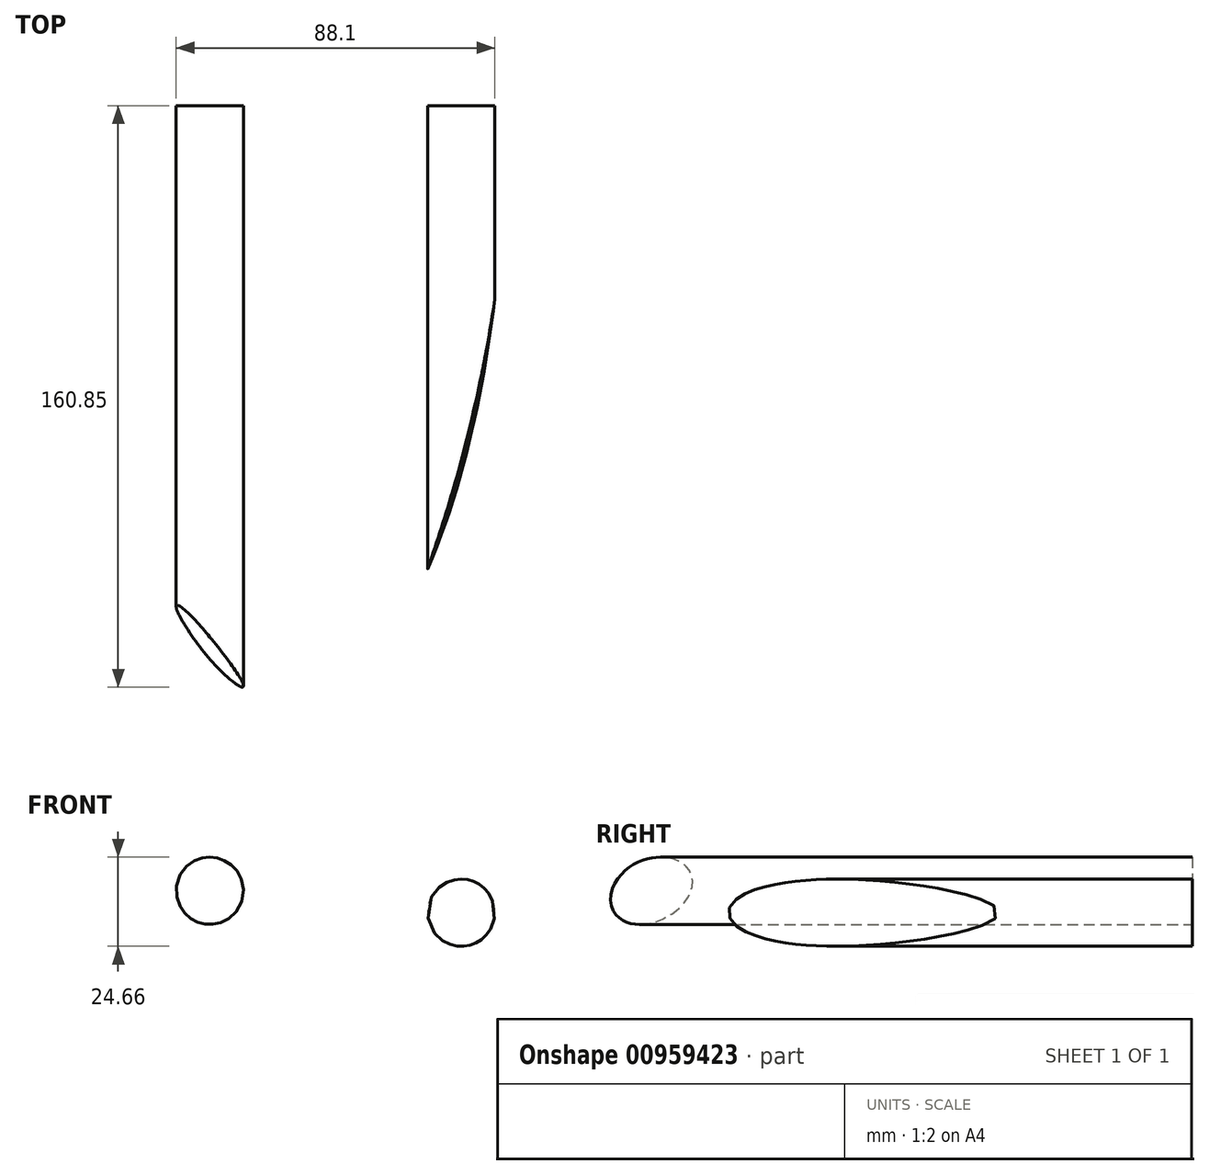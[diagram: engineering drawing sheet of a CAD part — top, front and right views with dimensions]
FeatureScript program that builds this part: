
annotation { "Feature Type Name" : "Feature", "Feature Type Description" : "" }
export const myFeature = defineFeature(function(context is Context, id is Id, definition is map)
    precondition{}
    {
        {
            var Q0;
            Q0=qCreatedBy(makeId("Front.planeOp"),FACE);
            var sketch = newSketch(context, id + "F0", { "sketchPlane" : qUnion([Q0])});
            skCircle(sketch, "E0", {"center": v(0, 0) * mm, "radius": 63.5 * mm});
            skLineSegment(sketch, "E1.0", {"start": v(40.6, 23.44) * mm, "end": v(40.6, -23.44) * mm, "construction": true});
            skLineSegment(sketch, "E1.1", {"start": v(40.6, -23.44) * mm, "end": v(0, -46.87) * mm, "construction": true});
            skLineSegment(sketch, "E1.2", {"start": v(0, -46.87) * mm, "end": v(-40.6, -23.44) * mm, "construction": true});
            skLineSegment(sketch, "E1.3", {"start": v(-40.6, -23.44) * mm, "end": v(-40.6, 23.44) * mm, "construction": true});
            skLineSegment(sketch, "E1.4", {"start": v(-40.6, 23.44) * mm, "end": v(0, 46.87) * mm, "construction": true});
            skLineSegment(sketch, "E1.5", {"start": v(0, 46.87) * mm, "end": v(40.6, 23.44) * mm, "construction": true});
            skPoint(sketch, "E1.0.midPoint", {"position": v(40.6, 0) * mm});
            skCircle(sketch, "E2", {"center": v(0, 0) * mm, "radius": 56.17 * mm, "construction": true});
            skCircle(sketch, "E3", {"center": v(0, 46.87) * mm, "radius": 9.3 * mm});
            skCircle(sketch, "E4", {"center": v(-40.6, 23.44) * mm, "radius": 9.3 * mm});
            skCircle(sketch, "E5", {"center": v(-40.6, -23.44) * mm, "radius": 9.3 * mm});
            skCircle(sketch, "E6", {"center": v(0, -46.87) * mm, "radius": 9.3 * mm});
            skCircle(sketch, "E7", {"center": v(40.6, -23.44) * mm, "radius": 9.3 * mm});
            skCircle(sketch, "E8", {"center": v(40.6, 23.44) * mm, "radius": 9.3 * mm});
            skCircle(sketch, "E9", {"center": v(-23.44, 40.6) * mm, "radius": 9.3 * mm});
            skCircle(sketch, "E10", {"center": v(-46.87, 0) * mm, "radius": 9.3 * mm});
            skCircle(sketch, "E11", {"center": v(-23.44, -40.6) * mm, "radius": 9.3 * mm});
            skLineSegment(sketch, "E12", {"start": v(-40.6, 23.44) * mm, "end": v(40.6, 23.44) * mm, "construction": true});
            skLineSegment(sketch, "E13", {"start": v(-40.6, -23.44) * mm, "end": v(40.6, -23.44) * mm, "construction": true});
            skCircle(sketch, "E14", {"center": v(23.44, 40.6) * mm, "radius": 9.3 * mm});
            skCircle(sketch, "E15", {"center": v(23.44, -40.6) * mm, "radius": 9.3 * mm});
            skCircle(sketch, "E16.MirrorC", {"center": v(46.87, 0) * mm, "radius": 9.3 * mm});
            skLineSegment(sketch, "E17", {"start": v(0, 0) * mm, "end": v(-28.09, 48.64) * mm});
            skLineSegment(sketch, "E18", {"start": v(0, 0) * mm, "end": v(28.09, -48.64) * mm});
            skLineSegment(sketch, "E19", {"start": v(0, 0) * mm, "end": v(-28.09, -48.64) * mm});
            skLineSegment(sketch, "E20", {"start": v(0, 0) * mm, "end": v(28.09, 48.64) * mm});
            skCircle(sketch, "E21", {"center": v(-22.64, 6.07) * mm, "radius": 9.3 * mm});
            skLineSegment(sketch, "E22.anchor1", {"start": v(0, 0) * mm, "end": v(-22.64, 6.07) * mm, "construction": true});
            skLineSegment(sketch, "E22.anchor2", {"start": v(0, 0) * mm, "end": v(-22.64, 6.07) * mm, "construction": true});
            skCircle(sketch, "E23.1.0", {"center": v(-16.57, -16.57) * mm, "radius": 9.3 * mm});
            skCircle(sketch, "E23.2.0", {"center": v(6.07, -22.64) * mm, "radius": 9.3 * mm});
            skCircle(sketch, "E24.1.3.0", {"center": v(22.64, -6.07) * mm, "radius": 9.3 * mm});
            skCircle(sketch, "E24.1.4.0", {"center": v(16.57, 16.57) * mm, "radius": 9.3 * mm});
            skCircle(sketch, "E24.1.5.0", {"center": v(-6.07, 22.64) * mm, "radius": 9.3 * mm});
            skSolve(sketch);
        }
        {
            var Q0;
            Q0=makeQuery(id+"F0.imprint","IMPRINT",FACE,{"disambiguationData":[TD([[makeQuery(id+"F0.imprint","IMPRINT",EDGE,{"derivedFrom":sQuery(id+"F0.wireOp",EDGE,"E10")}),1.0]])]});
            var Q1;
            Q1=makeQuery(id+"F0.imprint","IMPRINT",FACE,{"disambiguationData":[TD([[makeQuery(id+"F0.imprint","IMPRINT",EDGE,{"derivedFrom":sQuery(id+"F0.wireOp",EDGE,"E5")}),1.0]])]});
            var Q2;
            {var subQ0=sQuery(id+"F0.wireOp",EDGE,"E19");var subQ1=sQuery(id+"F0.wireOp",EDGE,"E11");var subQ2=makeQuery(id+"F0.imprint","INTERSECT",VERTEX,{"disambiguationData":[OD(0.0)],"derivedFrom":[subQ1,subQ0]});Q2=makeQuery(id+"F0.imprint","IMPRINT",FACE,{"disambiguationData":[TD([[makeQuery(id+"F0.imprint","IMPRINT",EDGE,{"disambiguationData":[TD([[subQ2,1.0]])],"derivedFrom":subQ1}),1.0]])]});}
            var Q3;
            {var subQ0=sQuery(id+"F0.wireOp",EDGE,"E19");var subQ1=sQuery(id+"F0.wireOp",EDGE,"E11");var subQ2=makeQuery(id+"F0.imprint","INTERSECT",VERTEX,{"disambiguationData":[OD(0.0)],"derivedFrom":[subQ1,subQ0]});Q3=makeQuery(id+"F0.imprint","IMPRINT",FACE,{"disambiguationData":[TD([[makeQuery(id+"F0.imprint","IMPRINT",EDGE,{"disambiguationData":[TD([[subQ2,-1.0]])],"derivedFrom":subQ1}),1.0]])]});}
            var Q4;
            Q4=makeQuery(id+"F0.imprint","IMPRINT",FACE,{"disambiguationData":[TD([[makeQuery(id+"F0.imprint","IMPRINT",EDGE,{"derivedFrom":sQuery(id+"F0.wireOp",EDGE,"E6")}),1.0]])]});
            var Q5;
            {var subQ0=sQuery(id+"F0.wireOp",EDGE,"E18");var subQ1=sQuery(id+"F0.wireOp",EDGE,"E15");var subQ2=makeQuery(id+"F0.imprint","INTERSECT",VERTEX,{"disambiguationData":[OD(0.0)],"derivedFrom":[subQ1,subQ0]});Q5=makeQuery(id+"F0.imprint","IMPRINT",FACE,{"disambiguationData":[TD([[makeQuery(id+"F0.imprint","IMPRINT",EDGE,{"disambiguationData":[TD([[subQ2,-1.0]])],"derivedFrom":subQ1}),1.0]])]});}
            var Q6;
            {var subQ0=sQuery(id+"F0.wireOp",EDGE,"E18");var subQ1=sQuery(id+"F0.wireOp",EDGE,"E15");var subQ2=makeQuery(id+"F0.imprint","INTERSECT",VERTEX,{"disambiguationData":[OD(0.0)],"derivedFrom":[subQ1,subQ0]});Q6=makeQuery(id+"F0.imprint","IMPRINT",FACE,{"disambiguationData":[TD([[makeQuery(id+"F0.imprint","IMPRINT",EDGE,{"disambiguationData":[TD([[subQ2,1.0]])],"derivedFrom":subQ1}),1.0]])]});}
            var Q7;
            Q7=makeQuery(id+"F0.imprint","IMPRINT",FACE,{"disambiguationData":[TD([[makeQuery(id+"F0.imprint","IMPRINT",EDGE,{"derivedFrom":sQuery(id+"F0.wireOp",EDGE,"E7")}),1.0]])]});
            var Q8;
            Q8=makeQuery(id+"F0.imprint","IMPRINT",FACE,{"disambiguationData":[TD([[makeQuery(id+"F0.imprint","IMPRINT",EDGE,{"derivedFrom":sQuery(id+"F0.wireOp",EDGE,"E16.MirrorC")}),-1.0]])]});
            var Q9;
            Q9=makeQuery(id+"F0.imprint","IMPRINT",FACE,{"disambiguationData":[TD([[makeQuery(id+"F0.imprint","IMPRINT",EDGE,{"derivedFrom":sQuery(id+"F0.wireOp",EDGE,"E8")}),1.0]])]});
            var Q10;
            {var subQ0=sQuery(id+"F0.wireOp",EDGE,"E20");var subQ1=sQuery(id+"F0.wireOp",EDGE,"E14");var subQ2=makeQuery(id+"F0.imprint","INTERSECT",VERTEX,{"disambiguationData":[OD(0.0)],"derivedFrom":[subQ1,subQ0]});Q10=makeQuery(id+"F0.imprint","IMPRINT",FACE,{"disambiguationData":[TD([[makeQuery(id+"F0.imprint","IMPRINT",EDGE,{"disambiguationData":[TD([[subQ2,1.0]])],"derivedFrom":subQ1}),1.0]])]});}
            var Q11;
            {var subQ0=sQuery(id+"F0.wireOp",EDGE,"E20");var subQ1=sQuery(id+"F0.wireOp",EDGE,"E14");var subQ2=makeQuery(id+"F0.imprint","INTERSECT",VERTEX,{"disambiguationData":[OD(0.0)],"derivedFrom":[subQ1,subQ0]});Q11=makeQuery(id+"F0.imprint","IMPRINT",FACE,{"disambiguationData":[TD([[makeQuery(id+"F0.imprint","IMPRINT",EDGE,{"disambiguationData":[TD([[subQ2,-1.0]])],"derivedFrom":subQ1}),1.0]])]});}
            var Q12;
            Q12=makeQuery(id+"F0.imprint","IMPRINT",FACE,{"disambiguationData":[TD([[makeQuery(id+"F0.imprint","IMPRINT",EDGE,{"derivedFrom":sQuery(id+"F0.wireOp",EDGE,"E3")}),1.0]])]});
            var Q13;
            {var subQ0=sQuery(id+"F0.wireOp",EDGE,"E17");var subQ1=sQuery(id+"F0.wireOp",EDGE,"E9");var subQ2=makeQuery(id+"F0.imprint","INTERSECT",VERTEX,{"disambiguationData":[OD(0.0)],"derivedFrom":[subQ1,subQ0]});Q13=makeQuery(id+"F0.imprint","IMPRINT",FACE,{"disambiguationData":[TD([[makeQuery(id+"F0.imprint","IMPRINT",EDGE,{"disambiguationData":[TD([[subQ2,-1.0]])],"derivedFrom":subQ1}),1.0]])]});}
            var Q14;
            {var subQ0=sQuery(id+"F0.wireOp",EDGE,"E17");var subQ1=sQuery(id+"F0.wireOp",EDGE,"E9");var subQ2=makeQuery(id+"F0.imprint","INTERSECT",VERTEX,{"disambiguationData":[OD(0.0)],"derivedFrom":[subQ1,subQ0]});Q14=makeQuery(id+"F0.imprint","IMPRINT",FACE,{"disambiguationData":[TD([[makeQuery(id+"F0.imprint","IMPRINT",EDGE,{"disambiguationData":[TD([[subQ2,1.0]])],"derivedFrom":subQ1}),1.0]])]});}
            var Q15;
            Q15=makeQuery(id+"F0.imprint","IMPRINT",FACE,{"disambiguationData":[TD([[makeQuery(id+"F0.imprint","IMPRINT",EDGE,{"derivedFrom":sQuery(id+"F0.wireOp",EDGE,"E4")}),1.0]])]});
            var Q16;
            Q16=makeQuery(id+"F0.imprint","IMPRINT",FACE,{"disambiguationData":[TD([[makeQuery(id+"F0.imprint","IMPRINT",EDGE,{"derivedFrom":sQuery(id+"F0.wireOp",EDGE,"E21")}),1.0]])]});
            var Q17;
            {var subQ0=sQuery(id+"F0.wireOp",EDGE,"E23.1.0");var subQ1=sQuery(id+"F0.wireOp",EDGE,"E19");var subQ2=makeQuery(id+"F0.imprint","INTERSECT",VERTEX,{"disambiguationData":[OD(0.0)],"derivedFrom":[subQ1,subQ0]});Q17=makeQuery(id+"F0.imprint","IMPRINT",FACE,{"disambiguationData":[TD([[makeQuery(id+"F0.imprint","IMPRINT",EDGE,{"disambiguationData":[TD([[subQ2,1.0]])],"derivedFrom":subQ1}),-1.0]])]});}
            var Q18;
            {var subQ0=sQuery(id+"F0.wireOp",EDGE,"E23.1.0");var subQ1=sQuery(id+"F0.wireOp",EDGE,"E19");var subQ2=makeQuery(id+"F0.imprint","INTERSECT",VERTEX,{"disambiguationData":[OD(0.0)],"derivedFrom":[subQ1,subQ0]});Q18=makeQuery(id+"F0.imprint","IMPRINT",FACE,{"disambiguationData":[TD([[makeQuery(id+"F0.imprint","IMPRINT",EDGE,{"disambiguationData":[TD([[subQ2,1.0]])],"derivedFrom":subQ1}),1.0]])]});}
            var Q19;
            {var subQ0=sQuery(id+"F0.wireOp",EDGE,"E23.2.0");var subQ1=sQuery(id+"F0.wireOp",EDGE,"E18");var subQ2=makeQuery(id+"F0.imprint","INTERSECT",VERTEX,{"disambiguationData":[OD(0.0)],"derivedFrom":[subQ1,subQ0]});Q19=makeQuery(id+"F0.imprint","IMPRINT",FACE,{"disambiguationData":[TD([[makeQuery(id+"F0.imprint","IMPRINT",EDGE,{"disambiguationData":[TD([[subQ2,-1.0]])],"derivedFrom":subQ1}),-1.0]])]});}
            var Q20;
            {var subQ0=sQuery(id+"F0.wireOp",EDGE,"E23.2.0");var subQ1=sQuery(id+"F0.wireOp",EDGE,"E18");var subQ2=makeQuery(id+"F0.imprint","INTERSECT",VERTEX,{"disambiguationData":[OD(0.0)],"derivedFrom":[subQ1,subQ0]});Q20=makeQuery(id+"F0.imprint","IMPRINT",FACE,{"disambiguationData":[TD([[makeQuery(id+"F0.imprint","IMPRINT",EDGE,{"disambiguationData":[TD([[subQ2,-1.0]])],"derivedFrom":subQ1}),1.0]])]});}
            var Q21;
            Q21=makeQuery(id+"F0.imprint","IMPRINT",FACE,{"disambiguationData":[TD([[makeQuery(id+"F0.imprint","IMPRINT",EDGE,{"derivedFrom":sQuery(id+"F0.wireOp",EDGE,"E24.1.3.0")}),1.0]])]});
            var Q22;
            {var subQ0=sQuery(id+"F0.wireOp",EDGE,"E24.1.4.0");var subQ1=sQuery(id+"F0.wireOp",EDGE,"E20");var subQ2=makeQuery(id+"F0.imprint","INTERSECT",VERTEX,{"disambiguationData":[OD(0.0)],"derivedFrom":[subQ1,subQ0]});Q22=makeQuery(id+"F0.imprint","IMPRINT",FACE,{"disambiguationData":[TD([[makeQuery(id+"F0.imprint","IMPRINT",EDGE,{"disambiguationData":[TD([[subQ2,-1.0]])],"derivedFrom":subQ1}),-1.0]])]});}
            var Q23;
            {var subQ0=sQuery(id+"F0.wireOp",EDGE,"E24.1.4.0");var subQ1=sQuery(id+"F0.wireOp",EDGE,"E20");var subQ2=makeQuery(id+"F0.imprint","INTERSECT",VERTEX,{"disambiguationData":[OD(0.0)],"derivedFrom":[subQ1,subQ0]});Q23=makeQuery(id+"F0.imprint","IMPRINT",FACE,{"disambiguationData":[TD([[makeQuery(id+"F0.imprint","IMPRINT",EDGE,{"disambiguationData":[TD([[subQ2,-1.0]])],"derivedFrom":subQ1}),1.0]])]});}
            var Q24;
            {var subQ0=sQuery(id+"F0.wireOp",EDGE,"E24.1.5.0");var subQ1=sQuery(id+"F0.wireOp",EDGE,"E17");var subQ2=makeQuery(id+"F0.imprint","INTERSECT",VERTEX,{"disambiguationData":[OD(0.0)],"derivedFrom":[subQ1,subQ0]});Q24=makeQuery(id+"F0.imprint","IMPRINT",FACE,{"disambiguationData":[TD([[makeQuery(id+"F0.imprint","IMPRINT",EDGE,{"disambiguationData":[TD([[subQ2,1.0]])],"derivedFrom":subQ1}),-1.0]])]});}
            var Q25;
            {var subQ0=sQuery(id+"F0.wireOp",EDGE,"E24.1.5.0");var subQ1=sQuery(id+"F0.wireOp",EDGE,"E17");var subQ2=makeQuery(id+"F0.imprint","INTERSECT",VERTEX,{"disambiguationData":[OD(0.0)],"derivedFrom":[subQ1,subQ0]});Q25=makeQuery(id+"F0.imprint","IMPRINT",FACE,{"disambiguationData":[TD([[makeQuery(id+"F0.imprint","IMPRINT",EDGE,{"disambiguationData":[TD([[subQ2,1.0]])],"derivedFrom":subQ1}),1.0]])]});}
            extrude(context, id + "F1", {"entities" : qUnion([Q0, Q1, Q2, Q3, Q4, Q5, Q6, Q7, Q8, Q9, Q10, Q11, Q12, Q13, Q14, Q15, Q16, Q17, Q18, Q19, Q20, Q21, Q22, Q23, Q24, Q25]), "depth" : 254 * mm, "offsetDistance" : 25.4 * mm});
        }
        {
            var Q0;
            Q0=qCreatedBy(makeId("Right.planeOp"),FACE);
            var sketch = newSketch(context, id + "F2", { "sketchPlane" : qUnion([Q0])});
            skLineSegment(sketch, "E25", {"start": v(0, 0) * mm, "end": v(0, 59.35) * mm});
            skEllipticalArc(sketch, "E26", {});
            skLineSegment(sketch, "E27", {"start": v(0, 0) * mm, "end": v(-165.62, 0) * mm});
            skPoint(sketch, "E28.orphan", {"position": v(165.62, 0) * mm});
            const initialGuessF2  = {"E26": [0, 0, 0, 1, 0.059354919940233224, 0.16561861336231232, 6.283185307179586, 1.5707963267948966]};
            skSetInitialGuess(sketch, initialGuessF2);
            skSolve(sketch);
        }
        {
            var Q0;
            Q0=makeQuery(id+"F2.imprint","IMPRINT",FACE,{"disambiguationData":[TD([[makeQuery(id+"F2.imprint","IMPRINT",EDGE,{"derivedFrom":sQuery(id+"F2.wireOp",EDGE,"E25")}),1.0]])]});
            var Q1;
            Q1=sQuery(id+"F2.wireOp",EDGE,"E27");
            revolve(context, id + "F3", {"surfaceOperationType" : NewSurfaceOperationType.NEW, "entities" : qUnion([Q0]), "axis" : qUnion([Q1]), "revolveType" : RevolveType.FULL});
        }
        {
            var Q0;
            Q0=makeQuery(id+"F1.opExtrude","SWEPT_BODY",BODY,{"disambiguationData":[OSD([sQuery(id+"F0.wireOp",EDGE,"E9")])]});
            var Q1;
            Q1=makeQuery(id+"F1.opExtrude","SWEPT_BODY",BODY,{"disambiguationData":[OSD([sQuery(id+"F0.wireOp",EDGE,"E4")])]});
            var Q2;
            Q2=makeQuery(id+"F1.opExtrude","SWEPT_BODY",BODY,{"disambiguationData":[OSD([sQuery(id+"F0.wireOp",EDGE,"E3")])]});
            var Q3;
            Q3=makeQuery(id+"F1.opExtrude","SWEPT_BODY",BODY,{"disambiguationData":[OSD([sQuery(id+"F0.wireOp",EDGE,"E14")])]});
            var Q4;
            Q4=makeQuery(id+"F1.opExtrude","SWEPT_BODY",BODY,{"disambiguationData":[OSD([sQuery(id+"F0.wireOp",EDGE,"E8")])]});
            var Q5;
            Q5=makeQuery(id+"F1.opExtrude","SWEPT_BODY",BODY,{"disambiguationData":[OSD([sQuery(id+"F0.wireOp",EDGE,"E24.1.4.0")])]});
            var Q6;
            Q6=makeQuery(id+"F1.opExtrude","SWEPT_BODY",BODY,{"disambiguationData":[OSD([sQuery(id+"F0.wireOp",EDGE,"E24.1.5.0")])]});
            var Q7;
            Q7=makeQuery(id+"F1.opExtrude","SWEPT_BODY",BODY,{"disambiguationData":[OSD([sQuery(id+"F0.wireOp",EDGE,"E21")])]});
            var Q8;
            Q8=makeQuery(id+"F1.opExtrude","SWEPT_BODY",BODY,{"disambiguationData":[OSD([sQuery(id+"F0.wireOp",EDGE,"E10")])]});
            var Q9;
            Q9=makeQuery(id+"F1.opExtrude","SWEPT_BODY",BODY,{"disambiguationData":[OSD([sQuery(id+"F0.wireOp",EDGE,"E16.MirrorC")])]});
            var Q10;
            Q10=makeQuery(id+"F1.opExtrude","SWEPT_BODY",BODY,{"disambiguationData":[OSD([sQuery(id+"F0.wireOp",EDGE,"E24.1.3.0")])]});
            var Q11;
            Q11=makeQuery(id+"F1.opExtrude","SWEPT_BODY",BODY,{"disambiguationData":[OSD([sQuery(id+"F0.wireOp",EDGE,"E23.1.0")])]});
            var Q12;
            Q12=makeQuery(id+"F1.opExtrude","SWEPT_BODY",BODY,{"disambiguationData":[OSD([sQuery(id+"F0.wireOp",EDGE,"E5")])]});
            var Q13;
            Q13=makeQuery(id+"F1.opExtrude","SWEPT_BODY",BODY,{"disambiguationData":[OSD([sQuery(id+"F0.wireOp",EDGE,"E11")])]});
            var Q14;
            Q14=makeQuery(id+"F1.opExtrude","SWEPT_BODY",BODY,{"disambiguationData":[OSD([sQuery(id+"F0.wireOp",EDGE,"E23.2.0")])]});
            var Q15;
            Q15=makeQuery(id+"F1.opExtrude","SWEPT_BODY",BODY,{"disambiguationData":[OSD([sQuery(id+"F0.wireOp",EDGE,"E7")])]});
            var Q16;
            Q16=makeQuery(id+"F1.opExtrude","SWEPT_BODY",BODY,{"disambiguationData":[OSD([sQuery(id+"F0.wireOp",EDGE,"E15")])]});
            var Q17;
            Q17=makeQuery(id+"F1.opExtrude","SWEPT_BODY",BODY,{"disambiguationData":[OSD([sQuery(id+"F0.wireOp",EDGE,"E6")])]});
            var Q18;
            Q18=makeQuery(id+"F3.opRevolve","SWEPT_BODY",BODY,{"disambiguationData":[OSD([sQuery(id+"F2.wireOp",EDGE,"E25"),sQuery(id+"F2.wireOp",EDGE,"E26"),sQuery(id+"F2.wireOp",EDGE,"E27")])]});
            booleanBodies(context, id + "F4", {"operationType" : BooleanOperationType.SUBTRACTION, "tools" : qUnion([Q0, Q1, Q2, Q3, Q4, Q5, Q6, Q7, Q8, Q9, Q10, Q11, Q12, Q13, Q14, Q15, Q16, Q17]), "targets" : qUnion([Q18])});
        }
    });
